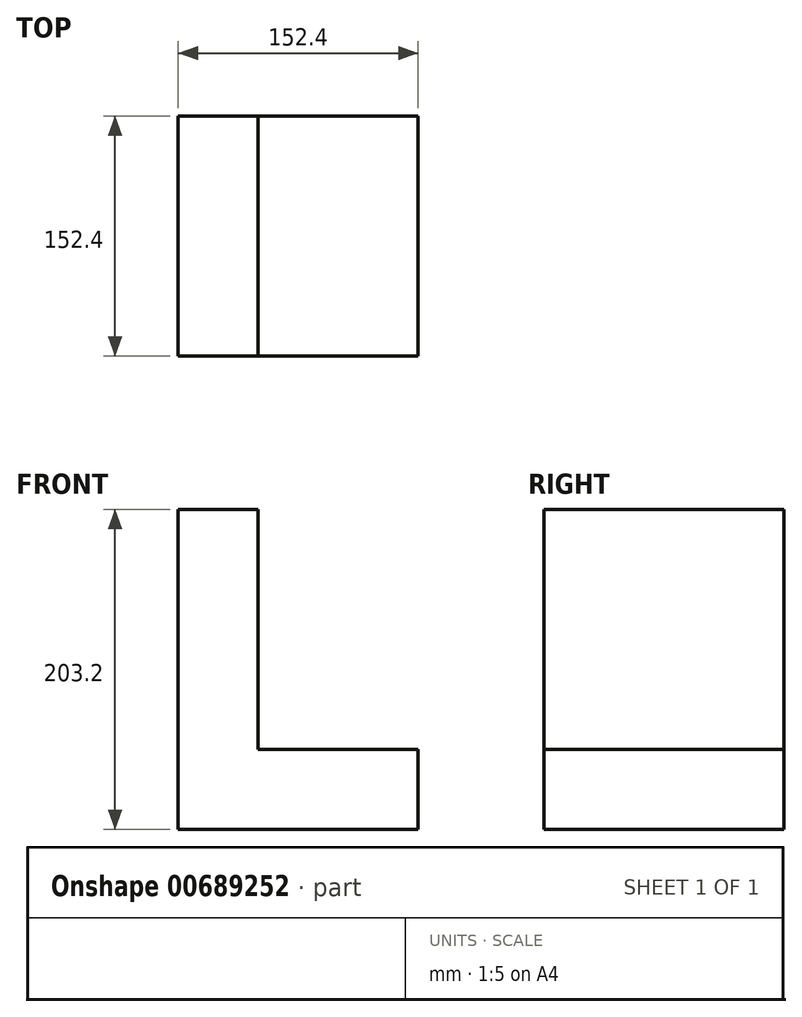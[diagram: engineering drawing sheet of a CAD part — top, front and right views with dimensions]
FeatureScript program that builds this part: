
annotation { "Feature Type Name" : "Feature", "Feature Type Description" : "" }
export const myFeature = defineFeature(function(context is Context, id is Id, definition is map)
    precondition{}
    {
        {
            var Q0;
            Q0=qCreatedBy(makeId("Front.planeOp"),FACE);
            var sketch = newSketch(context, id + "F0", { "sketchPlane" : qUnion([Q0])});
            skLineSegment(sketch, "E0", {"start": v(-100.43, 82.1) * mm, "end": v(-100.43, -121.1) * mm});
            skLineSegment(sketch, "E1", {"start": v(-100.43, -121.1) * mm, "end": v(51.97, -121.1) * mm});
            skLineSegment(sketch, "E2", {"start": v(51.97, -121.1) * mm, "end": v(51.97, -70.3) * mm});
            skLineSegment(sketch, "E3", {"start": v(51.97, -70.3) * mm, "end": v(-49.63, -70.3) * mm});
            skLineSegment(sketch, "E4", {"start": v(-49.63, -70.3) * mm, "end": v(-49.63, 82.1) * mm});
            skLineSegment(sketch, "E5", {"start": v(-49.63, 82.1) * mm, "end": v(-100.43, 82.1) * mm});
            skSolve(sketch);
        }
        {
            var Q0;
            Q0=makeQuery(id+"F0.imprint","IMPRINT",FACE,{"disambiguationData":[TD([[makeQuery(id+"F0.imprint","IMPRINT",EDGE,{"derivedFrom":sQuery(id+"F0.wireOp",EDGE,"E0")}),1.0]])]});
            extrude(context, id + "F1", {"entities" : qUnion([Q0]), "depth" : 152.4 * mm, "offsetDistance" : 25.4 * mm});
        }
    });
